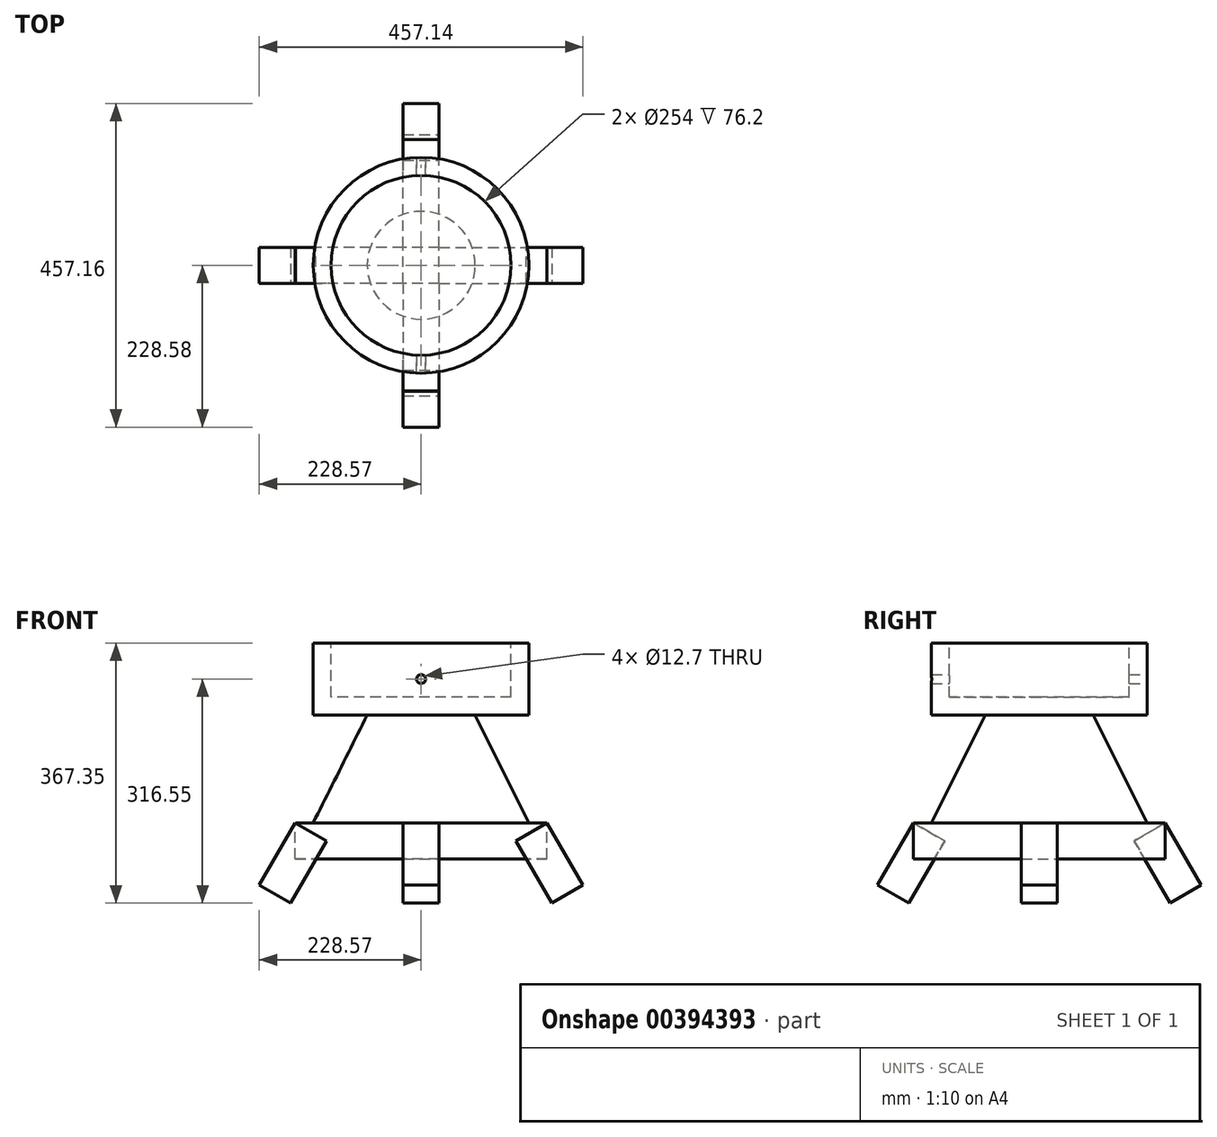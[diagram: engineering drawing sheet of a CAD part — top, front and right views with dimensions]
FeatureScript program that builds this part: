
annotation { "Feature Type Name" : "Feature", "Feature Type Description" : "" }
export const myFeature = defineFeature(function(context is Context, id is Id, definition is map)
    precondition{}
    {
        {
            var Q0;
            Q0=qCreatedBy(makeId("Top.planeOp"),FACE);
            var sketch = newSketch(context, id + "F0", { "sketchPlane" : qUnion([Q0])});
            skCircle(sketch, "E0", {"center": v(0, 0) * mm, "radius": 127 * mm});
            skCircle(sketch, "E1", {"center": v(0, 0) * mm, "radius": 152.4 * mm});
            skSolve(sketch);
        }
        {
            var Q0;
            Q0=makeQuery(id+"F0.imprint","IMPRINT",FACE,{"disambiguationData":[TD([[makeQuery(id+"F0.imprint","IMPRINT",EDGE,{"derivedFrom":sQuery(id+"F0.wireOp",EDGE,"E0")}),-1.0]])]});
            var Q1;
            Q1=makeQuery(id+"F0.imprint","IMPRINT",FACE,{"disambiguationData":[TD([[makeQuery(id+"F0.imprint","IMPRINT",EDGE,{"derivedFrom":sQuery(id+"F0.wireOp",EDGE,"E0")}),1.0]])]});
            extrude(context, id + "F1", {"entities" : qUnion([Q0, Q1]), "endBound" : BoundingType.SYMMETRIC, "depth" : 101.6 * mm});
        }
        {
            var Q0;
            Q0=qCreatedBy(makeId("Front.planeOp"),FACE);
            cPlane(context, id + "F2", {"entities" : qUnion([Q0]), "cplaneType" : CPlaneType.OFFSET, "offset" : 152.4 * mm, "width" : 152.4 * mm, "height" : 152.4 * mm});
        }
        {
            var Q0;
            Q0=qCreatedBy(id+"F2.planeOp",FACE);
            var sketch = newSketch(context, id + "F3", { "sketchPlane" : qUnion([Q0])});
            skCircle(sketch, "E2", {"center": v(0, 0) * mm, "radius": 6.35 * mm});
            skSolve(sketch);
        }
        {
            var Q0;
            Q0=makeQuery(id+"F3.imprint","IMPRINT",FACE,{"disambiguationData":[TD([[makeQuery(id+"F3.imprint","IMPRINT",EDGE,{"derivedFrom":sQuery(id+"F3.wireOp",EDGE,"E2")}),1.0]])]});
            extrude(context, id + "F4", {"entities" : qUnion([Q0]), "operationType" : NewBodyOperationType.REMOVE, "endBound" : BoundingType.THROUGH_ALL, "oppositeDirection" : true, "depth" : 25.4 * mm});
        }
        {
            var Q0;
            Q0=makeQuery(id+"F1.opExtrude","CAP_FACE",FACE,{"disambiguationData":[OSD([sQuery(id+"F0.wireOp",EDGE,"E1")])],"isStart":false});
            var sketch = newSketch(context, id + "F5", { "sketchPlane" : qUnion([Q0])});
            skCircle(sketch, "E3", {"center": v(0, 0) * mm, "radius": 127 * mm});
            skSolve(sketch);
        }
        {
            var Q0;
            Q0=makeQuery(id+"F5.imprint","IMPRINT",FACE,{"disambiguationData":[TD([[makeQuery(id+"F5.imprint","IMPRINT",EDGE,{"derivedFrom":sQuery(id+"F5.wireOp",EDGE,"E3")}),1.0]])]});
            extrude(context, id + "F6", {"entities" : qUnion([Q0]), "operationType" : NewBodyOperationType.REMOVE, "oppositeDirection" : true, "depth" : 76.2 * mm});
        }
        {
            var Q0;
            Q0=makeQuery(id+"F1.opExtrude","CAP_FACE",FACE,{"disambiguationData":[OSD([sQuery(id+"F0.wireOp",EDGE,"E1")])],"isStart":true});
            var sketch = newSketch(context, id + "F7", { "sketchPlane" : qUnion([Q0])});
            skCircle(sketch, "E4", {"center": v(0, 0) * mm, "radius": 76.2 * mm});
            skSolve(sketch);
        }
        {
            var Q0;
            Q0=qCreatedBy(makeId("Top.planeOp"),FACE);
            cPlane(context, id + "F8", {"entities" : qUnion([Q0]), "cplaneType" : CPlaneType.OFFSET, "offset" : 203.2 * mm, "oppositeDirection" : true, "width" : 152.4 * mm, "height" : 152.4 * mm});
        }
        {
            var Q0;
            Q0=qCreatedBy(id+"F8.planeOp",FACE);
            var sketch = newSketch(context, id + "F9", { "sketchPlane" : qUnion([Q0])});
            skCircle(sketch, "E5", {"center": v(0, 0) * mm, "radius": 152.4 * mm});
            skSolve(sketch);
        }
        {
            var Q1;
            Q1=makeQuery(id+"F7.imprint","IMPRINT",FACE,{"disambiguationData":[TD([[makeQuery(id+"F7.imprint","IMPRINT",EDGE,{"derivedFrom":sQuery(id+"F7.wireOp",EDGE,"E4")}),1.0]])]});
            var Q2;
            Q2=makeQuery(id+"F9.imprint","IMPRINT",FACE,{"disambiguationData":[TD([[makeQuery(id+"F9.imprint","IMPRINT",EDGE,{"derivedFrom":sQuery(id+"F9.wireOp",EDGE,"E5")}),1.0]])]});
            loft(context, id + "F10", {"operationType" : NewBodyOperationType.ADD, "sheetProfilesArray" : [{ "sheetProfileEntities" : qUnion([Q1]) }, { "sheetProfileEntities" : qUnion([Q2]) }]});
        }
        {
            var Q0;
            Q0=makeQuery(id+"F10.opLoft","CAP_FACE",FACE,{"disambiguationData":[OSD([makeQuery(id+"F9.imprint","IMPRINT",FACE,{"disambiguationData":[TD([[makeQuery(id+"F9.imprint","IMPRINT",EDGE,{"derivedFrom":sQuery(id+"F9.wireOp",EDGE,"E5")}),1.0]])]})])],"isStart":true});
            var sketch = newSketch(context, id + "F11", { "sketchPlane" : qUnion([Q0])});
            skLineSegment(sketch, "E6", {"start": v(0, 0) * mm, "end": v(0, 25.4) * mm});
            skLineSegment(sketch, "E7", {"start": v(0, 0) * mm, "end": v(0, -25.4) * mm});
            skLineSegment(sketch, "E8", {"start": v(0, -25.4) * mm, "end": v(0, -177.8) * mm});
            skLineSegment(sketch, "E9", {"start": v(0, 0) * mm, "end": v(0, 177.8) * mm});
            skLineSegment(sketch, "E10", {"start": v(0, 0) * mm, "end": v(177.8, 0) * mm});
            skLineSegment(sketch, "E11", {"start": v(0, 0) * mm, "end": v(-177.8, 0) * mm});
            skLineSegment(sketch, "E12.bottom", {"start": v(0, 25.4) * mm, "end": v(-25.4, 25.4) * mm});
            skLineSegment(sketch, "E12.top", {"start": v(0, 177.8) * mm, "end": v(-25.4, 177.8) * mm});
            skLineSegment(sketch, "E12.left", {"start": v(0, 25.4) * mm, "end": v(0, 177.8) * mm});
            skLineSegment(sketch, "E12.right", {"start": v(-25.4, 25.4) * mm, "end": v(-25.4, 177.8) * mm});
            skPoint(sketch, "E13.oppositeSnap0", {"position": v(-12.7, 177.8) * mm});
            skLineSegment(sketch, "E13.bottom", {"start": v(0, 25.4) * mm, "end": v(25.4, 25.4) * mm});
            skLineSegment(sketch, "E13.top", {"start": v(0, 177.8) * mm, "end": v(25.4, 177.8) * mm});
            skLineSegment(sketch, "E13.right", {"start": v(25.4, 25.4) * mm, "end": v(25.4, 177.8) * mm});
            skLineSegment(sketch, "E14", {"start": v(0, 0) * mm, "end": v(-25.4, 0) * mm});
            skLineSegment(sketch, "E15.bottom", {"start": v(-25.4, 0) * mm, "end": v(-177.8, 0) * mm});
            skLineSegment(sketch, "E15.top", {"start": v(-25.4, -25.4) * mm, "end": v(-177.8, -25.4) * mm});
            skLineSegment(sketch, "E15.left", {"start": v(-25.4, 0) * mm, "end": v(-25.4, -25.4) * mm});
            skLineSegment(sketch, "E15.right", {"start": v(-177.8, 0) * mm, "end": v(-177.8, -25.4) * mm});
            skLineSegment(sketch, "E16.top", {"start": v(-25.4, 25.4) * mm, "end": v(-177.8, 25.4) * mm});
            skLineSegment(sketch, "E16.left", {"start": v(-25.4, 0) * mm, "end": v(-25.4, 25.4) * mm});
            skLineSegment(sketch, "E16.right", {"start": v(-177.8, 0) * mm, "end": v(-177.8, 25.4) * mm});
            skLineSegment(sketch, "E17.bottom", {"start": v(25.4, 0) * mm, "end": v(177.8, 0) * mm});
            skLineSegment(sketch, "E17.top", {"start": v(25.4, 25.4) * mm, "end": v(177.8, 25.4) * mm});
            skLineSegment(sketch, "E17.left", {"start": v(25.4, 0) * mm, "end": v(25.4, 25.4) * mm});
            skLineSegment(sketch, "E17.right", {"start": v(177.8, 0) * mm, "end": v(177.8, 25.4) * mm});
            skLineSegment(sketch, "E18.top", {"start": v(25.4, -25.4) * mm, "end": v(177.8, -25.4) * mm});
            skLineSegment(sketch, "E18.left", {"start": v(25.4, 0) * mm, "end": v(25.4, -25.4) * mm});
            skLineSegment(sketch, "E18.right", {"start": v(177.8, 0) * mm, "end": v(177.8, -25.4) * mm});
            skSolve(sketch);
        }
        {
            var Q0;
            Q0=qCreatedBy(makeId("Front.planeOp"),FACE);
            var Q1;
            Q1=sQuery(id+"F11.wireOp",VERTEX,"E10.start");
            cPlane(context, id + "F12", {"entities" : qUnion([Q0, Q1]), "cplaneType" : CPlaneType.PLANE_POINT, "offset" : 25.4 * mm, "width" : 152.4 * mm, "height" : 152.4 * mm});
        }
        {
            var Q0;
            Q0=qCreatedBy(id+"F12.planeOp",FACE);
            cPlane(context, id + "F13", {"entities" : qUnion([Q0]), "cplaneType" : CPlaneType.OFFSET, "offset" : 177.8 * mm, "width" : 152.4 * mm, "height" : 152.4 * mm});
        }
        {
            var Q0;
            {var subQ0=sQuery(id+"F11.wireOp",EDGE,"E12.top");Q0=makeQuery(id+"F11.imprint","IMPRINT",FACE,{"disambiguationData":[TD([[makeQuery(id+"F11.imprint","IMPRINT",EDGE,{"derivedFrom":subQ0}),1.0]])]});}
            var Q1;
            {var subQ0=sQuery(id+"F11.wireOp",EDGE,"E13.top");Q1=makeQuery(id+"F11.imprint","IMPRINT",FACE,{"disambiguationData":[TD([[makeQuery(id+"F11.imprint","IMPRINT",EDGE,{"derivedFrom":subQ0}),-1.0]])]});}
            var Q2;
            {var subQ0=sQuery(id+"F11.wireOp",EDGE,"E12.bottom");Q2=makeQuery(id+"F11.imprint","IMPRINT",FACE,{"disambiguationData":[TD([[makeQuery(id+"F11.imprint","IMPRINT",EDGE,{"derivedFrom":subQ0}),-1.0]])]});}
            var Q3;
            {var subQ0=sQuery(id+"F11.wireOp",EDGE,"E13.bottom");Q3=makeQuery(id+"F11.imprint","IMPRINT",FACE,{"disambiguationData":[TD([[makeQuery(id+"F11.imprint","IMPRINT",EDGE,{"derivedFrom":subQ0}),1.0]])]});}
            extrude(context, id + "F14", {"entities" : qUnion([Q0, Q1, Q2, Q3]), "operationType" : NewBodyOperationType.ADD, "depth" : 50.8 * mm});
        }
        {
            var Q0;
            Q0=makeQuery(id+"F1.opExtrude","SWEPT_BODY",BODY,{"disambiguationData":[OSD([sQuery(id+"F0.wireOp",EDGE,"E1")])]});
            var Q1;
            Q1=qCreatedBy(id+"F12.planeOp",FACE);
            mirror(context, id + "F15", {"operationType" : NewBodyOperationType.ADD, "entities" : qUnion([Q0]), "mirrorPlane" : qUnion([Q1])});
        }
        {
            var Q0;
            {var subQ0=sQuery(id+"F11.wireOp",EDGE,"E15.right");Q0=makeQuery(id+"F11.imprint","IMPRINT",FACE,{"disambiguationData":[TD([[makeQuery(id+"F11.imprint","IMPRINT",EDGE,{"derivedFrom":subQ0}),1.0]])]});}
            var Q1;
            {var subQ0=sQuery(id+"F11.wireOp",EDGE,"E16.right");Q1=makeQuery(id+"F11.imprint","IMPRINT",FACE,{"disambiguationData":[TD([[makeQuery(id+"F11.imprint","IMPRINT",EDGE,{"derivedFrom":subQ0}),-1.0]])]});}
            var Q2;
            {var subQ0=sQuery(id+"F11.wireOp",EDGE,"E15.left");Q2=makeQuery(id+"F11.imprint","IMPRINT",FACE,{"disambiguationData":[TD([[makeQuery(id+"F11.imprint","IMPRINT",EDGE,{"derivedFrom":subQ0}),-1.0]])]});}
            var Q3;
            {var subQ0=sQuery(id+"F11.wireOp",EDGE,"E16.left");Q3=makeQuery(id+"F11.imprint","IMPRINT",FACE,{"disambiguationData":[TD([[makeQuery(id+"F11.imprint","IMPRINT",EDGE,{"derivedFrom":subQ0}),1.0]])]});}
            extrude(context, id + "F16", {"entities" : qUnion([Q0, Q1, Q2, Q3]), "depth" : 50.8 * mm});
        }
        {
            var Q0;
            {var subQ0=sQuery(id+"F11.wireOp",EDGE,"E18.left");Q0=makeQuery(id+"F11.imprint","IMPRINT",FACE,{"disambiguationData":[TD([[makeQuery(id+"F11.imprint","IMPRINT",EDGE,{"derivedFrom":subQ0}),1.0]])]});}
            var Q1;
            {var subQ0=sQuery(id+"F11.wireOp",EDGE,"E17.left");Q1=makeQuery(id+"F11.imprint","IMPRINT",FACE,{"disambiguationData":[TD([[makeQuery(id+"F11.imprint","IMPRINT",EDGE,{"derivedFrom":subQ0}),-1.0]])]});}
            var Q2;
            {var subQ0=sQuery(id+"F11.wireOp",EDGE,"E17.right");Q2=makeQuery(id+"F11.imprint","IMPRINT",FACE,{"disambiguationData":[TD([[makeQuery(id+"F11.imprint","IMPRINT",EDGE,{"derivedFrom":subQ0}),1.0]])]});}
            var Q3;
            {var subQ0=sQuery(id+"F11.wireOp",EDGE,"E18.right");Q3=makeQuery(id+"F11.imprint","IMPRINT",FACE,{"disambiguationData":[TD([[makeQuery(id+"F11.imprint","IMPRINT",EDGE,{"derivedFrom":subQ0}),-1.0]])]});}
            extrude(context, id + "F17", {"entities" : qUnion([Q0, Q1, Q2, Q3]), "depth" : 50.8 * mm});
        }
        {
            var Q0;
            Q0=qCreatedBy(id+"F13.planeOp",FACE);
            var Q1;
            Q1=sQuery(id+"F11.wireOp",EDGE,"E13.top");
            cPlane(context, id + "F18", {"entities" : qUnion([Q0, Q1]), "cplaneType" : CPlaneType.LINE_ANGLE, "offset" : 25.4 * mm, "angle" : 30 * degree, "oppositeDirection" : true, "width" : 152.4 * mm, "height" : 152.4 * mm});
        }
        {
            var Q0;
            Q0=qCreatedBy(id+"F18.planeOp",FACE);
            var sketch = newSketch(context, id + "F19", { "sketchPlane" : qUnion([Q0])});
            skLineSegment(sketch, "E19", {"start": v(25.52, -366.43) * mm, "end": v(-25.28, -366.43) * mm});
            skLineSegment(sketch, "E20", {"start": v(25.52, -366.43) * mm, "end": v(25.52, -264.83) * mm});
            skLineSegment(sketch, "E21", {"start": v(-25.28, -366.43) * mm, "end": v(-25.28, -264.83) * mm});
            skLineSegment(sketch, "E22", {"start": v(-25.28, -264.83) * mm, "end": v(25.52, -264.83) * mm});
            skSolve(sketch);
        }
        {
            var Q0;
            Q0=makeQuery(id+"F19.imprint","IMPRINT",FACE,{"disambiguationData":[TD([[makeQuery(id+"F19.imprint","IMPRINT",EDGE,{"derivedFrom":sQuery(id+"F19.wireOp",EDGE,"E19")}),-1.0]])]});
            extrude(context, id + "F20", {"entities" : qUnion([Q0]), "operationType" : NewBodyOperationType.ADD, "depth" : 50.8 * mm});
        }
        {
            var Q0;
            Q0=makeQuery(id+"F1.opExtrude","SWEPT_BODY",BODY,{"disambiguationData":[OSD([sQuery(id+"F0.wireOp",EDGE,"E1")])]});
            var Q1;
            Q1=qCreatedBy(id+"F12.planeOp",FACE);
            mirror(context, id + "F21", {"entities" : qUnion([Q0]), "mirrorPlane" : qUnion([Q1])});
        }
        {
            var Q0;
            Q0=qCreatedBy(makeId("Right.planeOp"),FACE);
            var Q1;
            Q1=sQuery(id+"F11.wireOp",VERTEX,"E6.start");
            cPlane(context, id + "F22", {"entities" : qUnion([Q0, Q1]), "cplaneType" : CPlaneType.PLANE_POINT, "offset" : 25.4 * mm, "width" : 152.4 * mm, "height" : 152.4 * mm});
        }
        {
            var Q0;
            Q0=qCreatedBy(id+"F22.planeOp",FACE);
            var Q1;
            Q1=sQuery(id+"F11.wireOp",EDGE,"E18.right");
            cPlane(context, id + "F23", {"entities" : qUnion([Q0, Q1]), "cplaneType" : CPlaneType.LINE_ANGLE, "offset" : 177.8 * mm, "angle" : 30 * degree, "oppositeDirection" : true, "width" : 152.4 * mm, "height" : 152.4 * mm});
        }
        {
            var Q0;
            Q0=qCreatedBy(id+"F23.planeOp",FACE);
            var sketch = newSketch(context, id + "F24", { "sketchPlane" : qUnion([Q0])});
            skLineSegment(sketch, "E23.bottom", {"start": v(-25.32, -264.82) * mm, "end": v(25.48, -264.82) * mm});
            skLineSegment(sketch, "E23.top", {"start": v(-25.32, -366.42) * mm, "end": v(25.48, -366.42) * mm});
            skLineSegment(sketch, "E23.left", {"start": v(-25.32, -264.82) * mm, "end": v(-25.32, -366.42) * mm});
            skLineSegment(sketch, "E23.right", {"start": v(25.48, -264.82) * mm, "end": v(25.48, -366.42) * mm});
            skSolve(sketch);
        }
        {
            var Q0;
            Q0=makeQuery(id+"F24.imprint","IMPRINT",FACE,{"disambiguationData":[TD([[makeQuery(id+"F24.imprint","IMPRINT",EDGE,{"derivedFrom":sQuery(id+"F24.wireOp",EDGE,"E23.bottom")}),-1.0]])]});
            extrude(context, id + "F25", {"entities" : qUnion([Q0]), "operationType" : NewBodyOperationType.ADD, "depth" : 50.8 * mm});
        }
        {
            var Q0;
            Q0=makeQuery(id+"F17.opExtrude","SWEPT_BODY",BODY,{"disambiguationData":[OSD([sQuery(id+"F11.wireOp",EDGE,"E17.top"),sQuery(id+"F11.wireOp",EDGE,"E17.left"),sQuery(id+"F11.wireOp",EDGE,"E17.right"),sQuery(id+"F11.wireOp",EDGE,"E18.top"),sQuery(id+"F11.wireOp",EDGE,"E18.left"),sQuery(id+"F11.wireOp",EDGE,"E18.right")])]});
            var Q1;
            Q1=qCreatedBy(id+"F22.planeOp",FACE);
            mirror(context, id + "F26", {"entities" : qUnion([Q0]), "mirrorPlane" : qUnion([Q1])});
        }
    });
